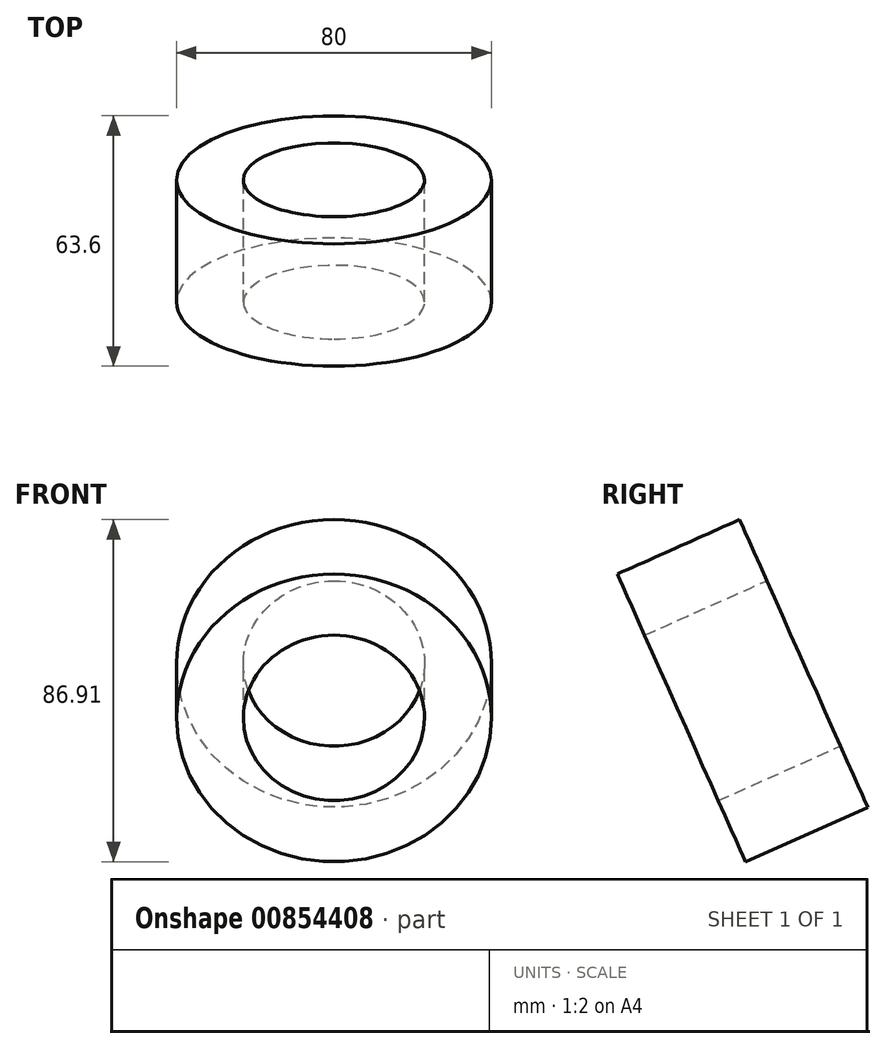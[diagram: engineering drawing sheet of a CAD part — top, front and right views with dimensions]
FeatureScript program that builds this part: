
annotation { "Feature Type Name" : "Feature", "Feature Type Description" : "" }
export const myFeature = defineFeature(function(context is Context, id is Id, definition is map)
    precondition{}
    {
        {
            var Q0;
            Q0=qCreatedBy(makeId("Top.planeOp"),FACE);
            var sketch = newSketch(context, id + "F0", { "sketchPlane" : qUnion([Q0])});
            skLineSegment(sketch, "E0", {"start": v(-31.54, 0) * mm, "end": v(35.6, 0) * mm});
            skSolve(sketch);
        }
        {
            var Q0;
            Q0=sQuery(id+"F0.wireOp",EDGE,"E0");
            cPlane(context, id + "F1", {"entities" : qUnion([Q0]), "cplaneType" : CPlaneType.LINE_ANGLE, "offset" : 25 * mm, "angle" : 24 * degree, "width" : 150 * mm, "height" : 150 * mm});
        }
        {
            var Q0;
            Q0=qCreatedBy(id+"F1.planeOp",FACE);
            var sketch = newSketch(context, id + "F2", { "sketchPlane" : qUnion([Q0])});
            skCircle(sketch, "E1", {"center": v(0, 0) * mm, "radius": 23 * mm});
            skCircle(sketch, "E2", {"center": v(0, 0) * mm, "radius": 40 * mm});
            skSolve(sketch);
        }
        {
            var Q0;
            Q0=qCreatedBy(makeId("Right.planeOp"),FACE);
            var sketch = newSketch(context, id + "F3", { "sketchPlane" : qUnion([Q0])});
            skLineSegment(sketch, "E3.0", {"start": v(-9.35, 21.01) * mm, "end": v(9.35, -21.01) * mm});
            skLineSegment(sketch, "E3.1", {"start": v(-16.27, 36.54) * mm, "end": v(16.27, -36.54) * mm});
            skLineSegment(sketch, "E4", {"start": v(-38.7, -65) * mm, "end": v(43.93, -65) * mm});
            skSolve(sketch);
        }
        {
            var Q0;
            Q0=makeQuery(id+"F2.imprint","IMPRINT",FACE,{"disambiguationData":[TD([[makeQuery(id+"F2.imprint","IMPRINT",EDGE,{"derivedFrom":sQuery(id+"F2.wireOp",EDGE,"E1")}),-1.0]])]});
            extrude(context, id + "F4", {"entities" : qUnion([Q0]), "oppositeDirection" : true, "depth" : 34 * mm, "offsetDistance" : 25 * mm});
        }
    });
